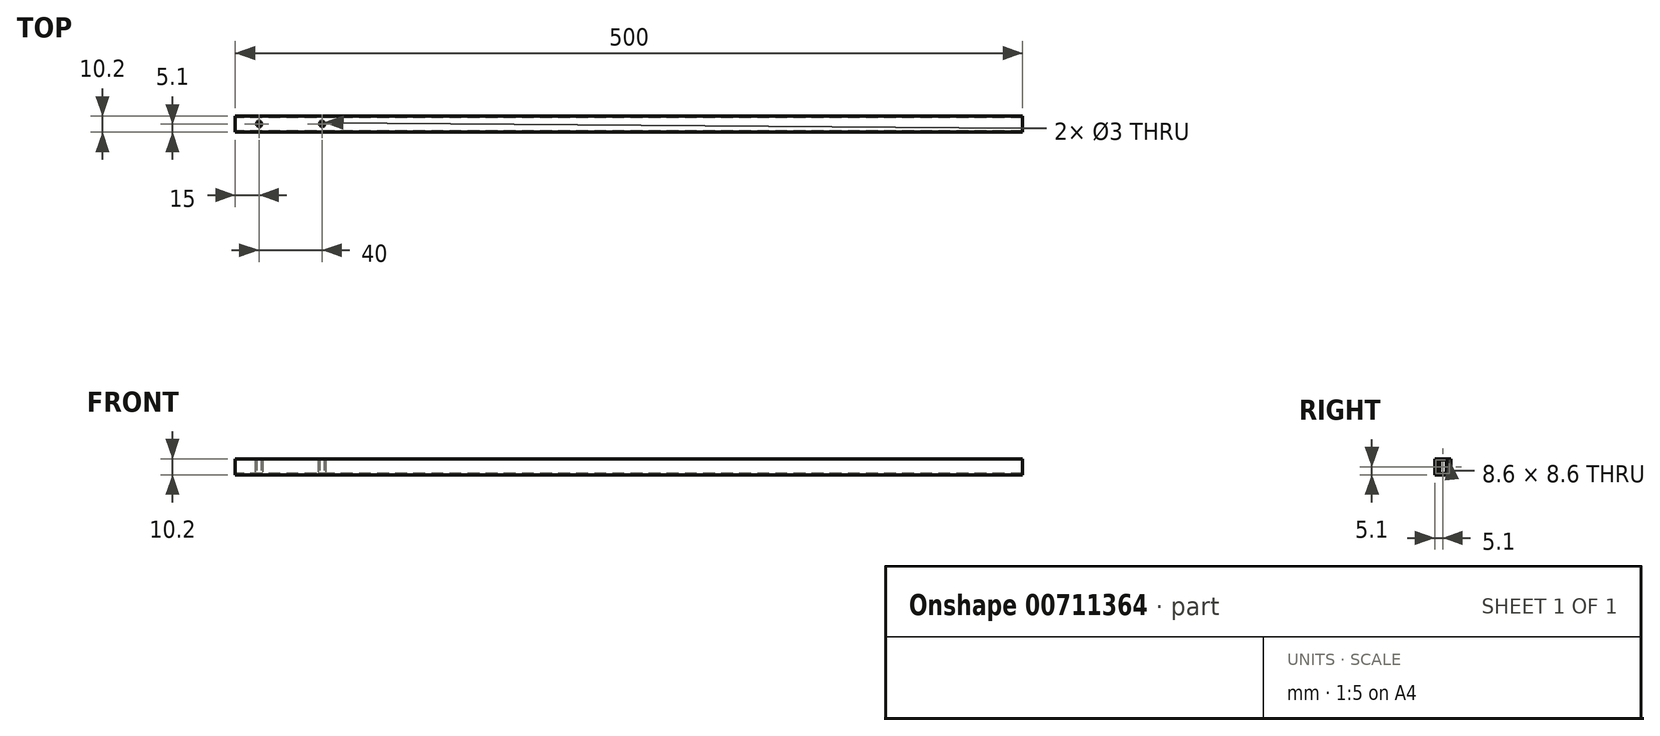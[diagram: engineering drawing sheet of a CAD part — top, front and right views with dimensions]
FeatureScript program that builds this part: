
annotation { "Feature Type Name" : "Feature", "Feature Type Description" : "" }
export const myFeature = defineFeature(function(context is Context, id is Id, definition is map)
    precondition{}
    {
        {
            var Q0;
            Q0=qCreatedBy(makeId("Top.planeOp"),FACE);
            var sketch = newSketch(context, id + "F0", { "sketchPlane" : qUnion([Q0])});
            skLineSegment(sketch, "E0.bottom", {"start": v(250, -5.1) * mm, "end": v(-250, -5.1) * mm});
            skLineSegment(sketch, "E0.top", {"start": v(250, 5.1) * mm, "end": v(-250, 5.1) * mm});
            skLineSegment(sketch, "E0.left", {"start": v(250, -5.1) * mm, "end": v(250, 5.1) * mm});
            skLineSegment(sketch, "E0.right", {"start": v(-250, -5.1) * mm, "end": v(-250, 5.1) * mm});
            skPoint(sketch, "E0.middle", {"position": v(0, 0) * mm});
            skPoint(sketch, "E1", {"position": v(-235, 0) * mm});
            skPoint(sketch, "E2", {"position": v(-195, 0) * mm});
            skCircle(sketch, "E3", {"center": v(-235, 0) * mm, "radius": 1.5 * mm});
            skCircle(sketch, "E4", {"center": v(-195, 0) * mm, "radius": 1.5 * mm});
            skSolve(sketch);
        }
        {
            var Q0;
            Q0=makeQuery(id+"F0.imprint","IMPRINT",FACE,{"disambiguationData":[TD([[makeQuery(id+"F0.imprint","IMPRINT",EDGE,{"derivedFrom":sQuery(id+"F0.wireOp",EDGE,"E0.bottom")}),-1.0]])]});
            extrude(context, id + "F1", {"entities" : qUnion([Q0]), "depth" : 10.2 * mm, "offsetDistance" : 25 * mm});
        }
        {
            var Q0;
            Q0=makeQuery(id+"F1.opExtrude","SWEPT_FACE",FACE,{"disambiguationData":[OSD([sQuery(id+"F0.wireOp",EDGE,"E0.left")])]});
            var Q1;
            Q1=makeQuery(id+"F1.opExtrude","SWEPT_FACE",FACE,{"disambiguationData":[OSD([sQuery(id+"F0.wireOp",EDGE,"E0.right")])]});
            shell(context, id + "F2", {"entities" : qUnion([Q0, Q1]), "thickness" : 0.8 * mm});
        }
    });
